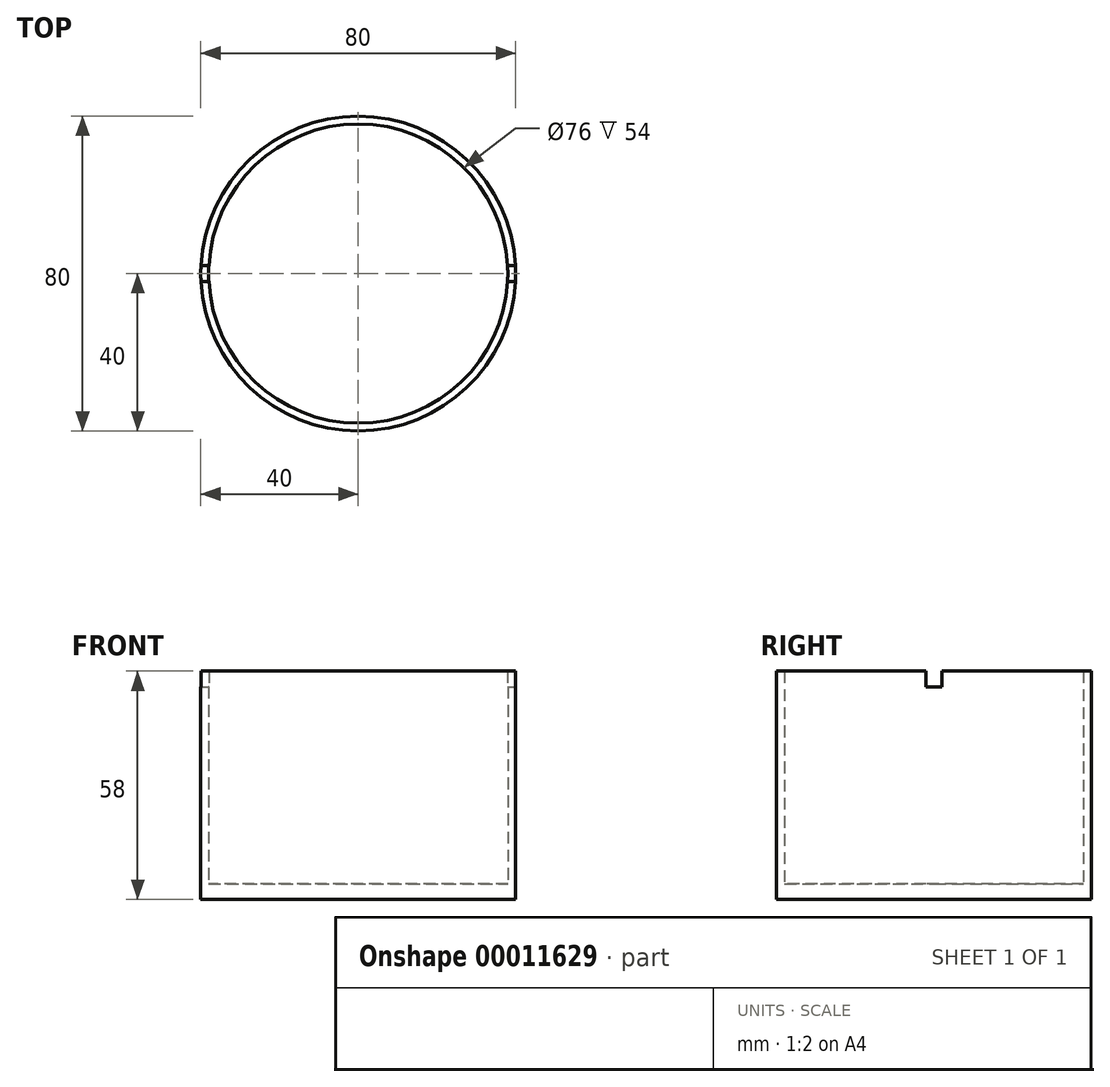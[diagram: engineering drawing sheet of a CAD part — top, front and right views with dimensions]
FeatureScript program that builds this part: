
annotation { "Feature Type Name" : "Feature", "Feature Type Description" : "" }
export const myFeature = defineFeature(function(context is Context, id is Id, definition is map)
    precondition{}
    {
        {
            var Q0;
            Q0=qCreatedBy(makeId("Top.planeOp"),FACE);
            var sketch = newSketch(context, id + "F0", { "sketchPlane" : qUnion([Q0])});
            skCircle(sketch, "E0", {"center": v(0, 0) * mm, "radius": 40 * mm});
            skCircle(sketch, "E1", {"center": v(0, 0) * mm, "radius": 38 * mm});
            skSolve(sketch);
        }
        {
            var Q0;
            Q0 = qSketchRegion(id + "F0", true);
            extrude(context, id + "F1", {"entities" : qUnion([Q0]), "depth" : 54 * mm});
        }
        {
            var Q0;
            Q0=makeQuery(id+"F0.imprint","IMPRINT",FACE,{"disambiguationData":[TD([[makeQuery(id+"F0.imprint","IMPRINT",EDGE,{"derivedFrom":sQuery(id+"F0.wireOp",EDGE,"E1")}),1.0]])]});
            var Q1;
            Q1=makeQuery(id+"F0.imprint","IMPRINT",FACE,{"disambiguationData":[TD([[makeQuery(id+"F0.imprint","IMPRINT",EDGE,{"derivedFrom":sQuery(id+"F0.wireOp",EDGE,"E0")}),1.0]])]});
            extrude(context, id + "F2", {"entities" : qUnion([Q0, Q1]), "operationType" : NewBodyOperationType.ADD, "oppositeDirection" : true, "depth" : 4 * mm});
        }
        {
            var Q0;
            Q0=qCreatedBy(makeId("Front.planeOp"),FACE);
            var sketch = newSketch(context, id + "F3", { "sketchPlane" : qUnion([Q0])});
            skLineSegment(sketch, "E2.bottom", {"start": v(-58.13, 54) * mm, "end": v(57.87, 54) * mm});
            skLineSegment(sketch, "E2.top", {"start": v(-58.13, 50) * mm, "end": v(57.87, 50) * mm});
            skLineSegment(sketch, "E2.left", {"start": v(-58.13, 54) * mm, "end": v(-58.13, 50) * mm});
            skLineSegment(sketch, "E2.right", {"start": v(57.87, 54) * mm, "end": v(57.87, 50) * mm});
            skSolve(sketch);
        }
        {
            var Q0;
            Q0 = qSketchRegion(id + "F3", true);
            extrude(context, id + "F4", {"entities" : qUnion([Q0]), "operationType" : NewBodyOperationType.REMOVE, "endBound" : BoundingType.SYMMETRIC, "oppositeDirection" : true, "depth" : 4 * mm});
        }
    });
